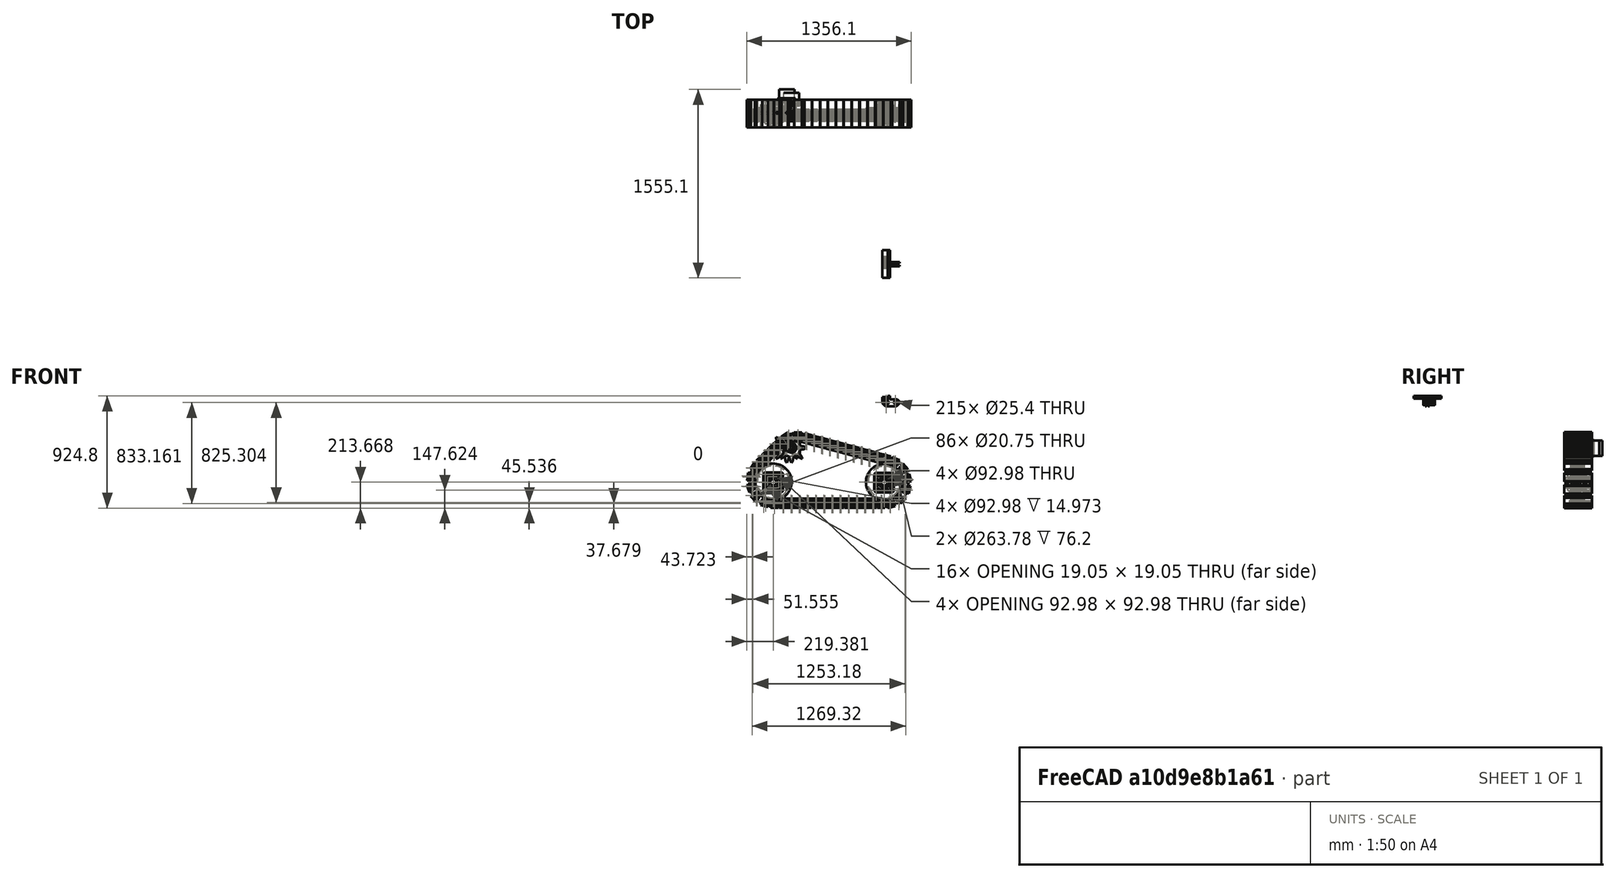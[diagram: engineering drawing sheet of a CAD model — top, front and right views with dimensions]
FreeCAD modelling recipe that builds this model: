
FCSTD DOCUMENT  (FreeCAD 0.16R6712 (Git))
Label: Track_CS 1
License: All rights reserved
LicenseURL: http://en.wikipedia.org/wiki/All_rights_reserved
objects: Part::Compound×4, Part::Feature×3, Sketcher::SketchObject×1, Part::FeaturePython×1, Part::Box×1, Part::MultiFuse×1
note: 11 computed .brp shape members not serialized (recipe doc carries the construction recipe); baked Part::Feature solids carry a one-line shape summary decoded from their .brp

FEATURE [Sketcher::SketchObject] Sketch  label="Track CS"
  Placement = pos=(1.51484e-06,1234.99,0.000147214) rot=(1,0,0;1.5708rad)
  sketch-geometry (16):
    g0: LineSegment StartX=-933.196 StartY=-844.354 StartZ=0 EndX=19.2626 EndY=-844.354 EndZ=0
    g1: LineSegment StartX=28.9329 StartY=-568.153 StartZ=0 EndX=-697.964 EndY=-373.418 EndZ=0
    g2: LineSegment StartX=-829.259 StartY=-408.704 StartZ=0 EndX=-1014.31 EndY=-593.608 EndZ=0
    g3: LineSegment StartX=-1053.26 StartY=-655.502 StartZ=0 EndX=-1060.21 EndY=-722.808 EndZ=0
    g4: LineSegment StartX=-1060.21 StartY=-722.808 StartZ=0 EndX=-1036.71 EndY=-786.97 EndZ=0
    g5: LineSegment StartX=-1036.71 StartY=-786.97 StartZ=0 EndX=-998.827 EndY=-826.454 EndZ=0
    g6: LineSegment StartX=-998.827 StartY=-826.454 StartZ=0 EndX=-933.196 EndY=-844.354 EndZ=0
    g7: LineSegment StartX=19.2626 StartY=-844.354 StartZ=0 EndX=79.1111 EndY=-829.446 EndZ=0
    g8: LineSegment StartX=79.1111 StartY=-829.446 StartZ=0 EndX=125.854 EndY=-776.15 EndZ=0
    g9: LineSegment StartX=139.885 StartY=-702.91 StartZ=0 EndX=121.744 EndY=-638.348 EndZ=0
    g10: LineSegment StartX=121.744 StartY=-638.348 StartZ=0 EndX=79.5894 EndY=-589.172 EndZ=0
    g11: LineSegment StartX=79.5894 StartY=-589.172 StartZ=0 EndX=28.9329 EndY=-568.153 EndZ=0
    g12: LineSegment StartX=-829.259 StartY=-408.704 StartZ=0 EndX=-772.427 EndY=-371.419 EndZ=0
    g13: LineSegment StartX=125.854 StartY=-776.15 StartZ=0 EndX=139.885 EndY=-702.91 EndZ=0
    g14: LineSegment StartX=-772.427 StartY=-371.419 StartZ=0 EndX=-697.964 EndY=-373.418 EndZ=0
    g15: LineSegment StartX=-1014.31 StartY=-593.608 StartZ=0 EndX=-1053.26 EndY=-655.502 EndZ=0
  constraints (18):
    c: Horizontal(g0)
    c: Coincident(g4,g3)
    c: Coincident(g6,g5)
    c: Coincident(g0,g6)
    c: DistanceY(g0) = -844.354
    c: Coincident(g11,g10)
    c: Coincident(g7,g0)
    c: Coincident(g13,g8)
    c: Coincident(g13,g9)
    c: Coincident(g4,g5)
    c: Coincident(g8,g7)
    c: Coincident(g10,g9)
    c: Coincident(g12,g2)
    c: Coincident(g1,g14)
    c: Coincident(g1,g11)
    c: Coincident(g15,g2)
    c: Coincident(g15,g3)
    c: Coincident(g12,g14)
FEATURE [Part::Compound] Compound027015  label="Track Unit"
  Placement = pos=(0,0,0) rot=(0.707107,0.707107,0;3.14159rad)
FEATURE [Part::FeaturePython] PathArray  # WARN: FeaturePython — macro-defined, semantics opaque (R4)
  Align = true
  Base = -> Compound027015
  Count = 42
  PathObj = -> Sketch
  Xlate = (0,-6.35,82.55)
FEATURE [Part::Box] Box  label="Cube"
  Height = 9.525
  Length = 19.05
  Placement = pos=(24.13,-114.3,-6.36567) rot=(0,0,1;0rad)
  Width = 228.6
FEATURE [Part::Compound] Compound027016  label="Track Unit001"
  Placement = pos=(0,0,0) rot=(0.707107,0.707107,0;3.14159rad)
FEATURE [Part::MultiFuse] Fusion
  Shapes = -> [Box,Compound027016]
FEATURE [Part::Feature] Fusion001  label="Track Unit 2"
  shape: bbox 142.2 x 228.6 x 85.73 mm, 138 faces, 7 solids (baked)
FEATURE [Part::Feature] Compound010002  label="15.9 cu in motor"
  Placement = pos=(-877.46,1333.1,-518.244) rot=(0,0,1;0rad)
  shape: bbox 248.4 x 213.9 x 248.4 mm, 198 faces, 8 solids (baked)
FEATURE [Part::Compound] Compound  label="Idler Front Right"
  Placement = pos=(51.403,1087.87,-861.972) rot=(0,0,1;3.14159rad)
FEATURE [Part::Compound] Compound002  label="Idler Rear Right"
  Placement = pos=(-863.25,1087.87,-860.249) rot=(0,0,1;3.14159rad)
FEATURE [Part::Feature] Compound001  label="15.9 cu in motor right"
  Placement = pos=(-837.967,1306.7,-518.244) rot=(0,0,1;0rad)
  shape: bbox 248.4 x 213.9 x 248.4 mm, 198 faces, 8 solids (baked)
